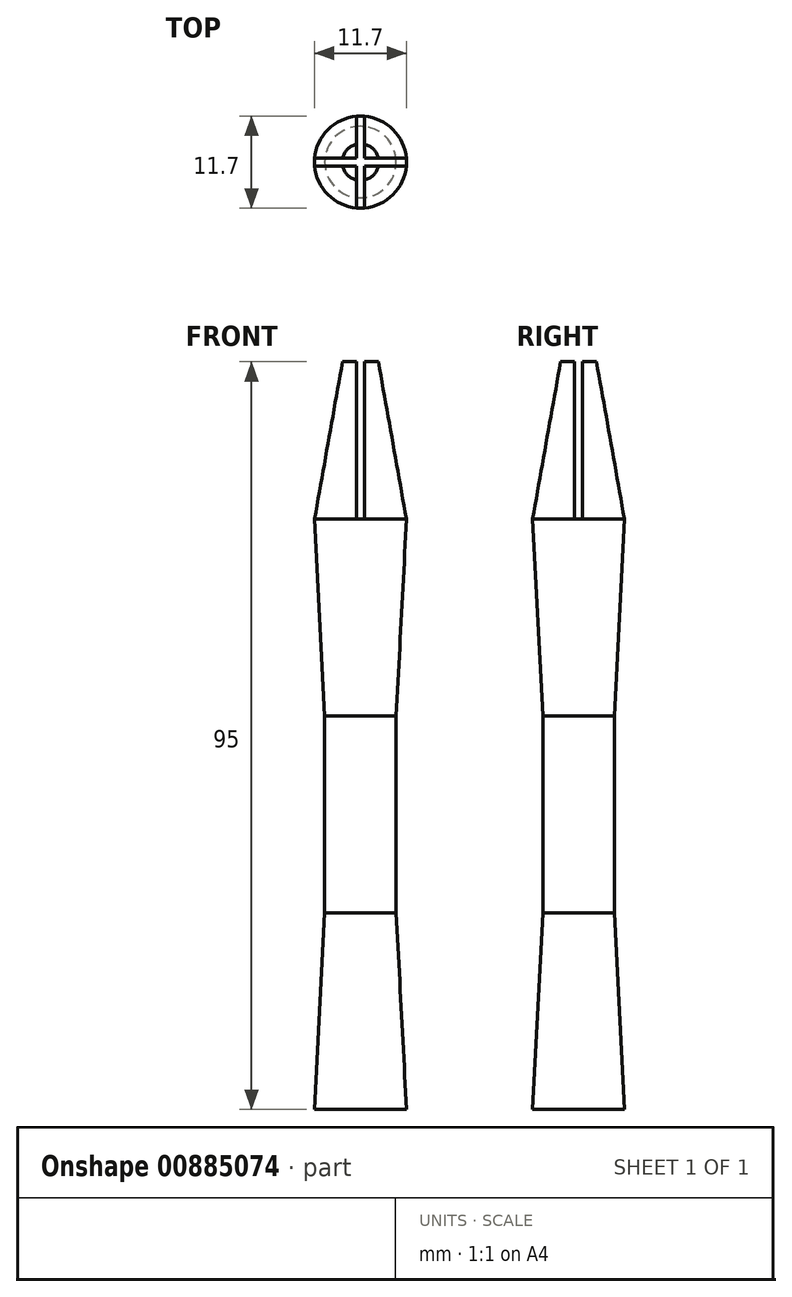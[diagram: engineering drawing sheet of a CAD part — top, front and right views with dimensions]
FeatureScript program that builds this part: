
annotation { "Feature Type Name" : "Feature", "Feature Type Description" : "" }
export const myFeature = defineFeature(function(context is Context, id is Id, definition is map)
    precondition{}
    {
        {
            var Q0;
            Q0=qCreatedBy(makeId("Top.planeOp"),FACE);
            var sketch = newSketch(context, id + "F0", { "sketchPlane" : qUnion([Q0])});
            skCircle(sketch, "E0", {"center": v(0, 0) * mm, "radius": 5.85 * mm});
            skSolve(sketch);
        }
        {
            var Q0;
            Q0=makeQuery(id+"F0.imprint","IMPRINT",FACE,{"disambiguationData":[TD([[makeQuery(id+"F0.imprint","IMPRINT",EDGE,{"derivedFrom":sQuery(id+"F0.wireOp",EDGE,"E0")}),1.0]])]});
            var Q1;
            Q1=sQuery(id+"F0.wireOp",EDGE,"E0");
            extrude(context, id + "F1", {"entities" : qUnion([Q0]), "surfaceEntities" : qUnion([Q1]), "depth" : 25 * mm, "offsetDistance" : 25 * mm, "hasDraft" : true, "draftAngle" : 3 * degree, "draftPullDirection" : true});
        }
        {
            var Q0;
            Q0=makeQuery(id+"F1.opExtrude","CAP_FACE",FACE,{"disambiguationData":[OSD([sQuery(id+"F0.wireOp",EDGE,"E0")])],"isStart":false});
            extrude(context, id + "F2", {"entities" : qUnion([Q0]), "operationType" : NewBodyOperationType.ADD, "depth" : 25 * mm, "offsetDistance" : 25 * mm});
        }
        {
            var Q0;
            Q0=makeQuery(id+"F2.opExtrude","CAP_FACE",FACE,{"disambiguationData":[OSD([sQuery(id+"F0.wireOp",EDGE,"E0")])],"isStart":false});
            extrude(context, id + "F3", {"entities" : qUnion([Q0]), "operationType" : NewBodyOperationType.ADD, "depth" : 25 * mm, "offsetDistance" : 25 * mm, "hasDraft" : true, "draftAngle" : 3 * degree});
        }
        {
            var Q0;
            Q0=makeQuery(id+"F3.opExtrude","CAP_FACE",FACE,{"disambiguationData":[OSD([sQuery(id+"F0.wireOp",EDGE,"E0")])],"isStart":false});
            extrude(context, id + "F4", {"entities" : qUnion([Q0]), "operationType" : NewBodyOperationType.ADD, "depth" : 20 * mm, "offsetDistance" : 25 * mm, "hasDraft" : true, "draftAngle" : 10 * degree, "draftPullDirection" : true});
        }
        {
            var Q0;
            Q0=makeQuery(id+"F4.opExtrude","CAP_FACE",FACE,{"disambiguationData":[OSD([sQuery(id+"F0.wireOp",EDGE,"E0")])],"isStart":false});
            var sketch = newSketch(context, id + "F5", { "sketchPlane" : qUnion([Q0])});
            skLineSegment(sketch, "E1.bottom", {"start": v(-10.12, -0.5) * mm, "end": v(10.12, -0.5) * mm});
            skLineSegment(sketch, "E1.top", {"start": v(-10.12, 0.5) * mm, "end": v(10.12, 0.5) * mm});
            skLineSegment(sketch, "E1.left", {"start": v(-10.12, -0.5) * mm, "end": v(-10.12, 0.5) * mm});
            skLineSegment(sketch, "E1.right", {"start": v(10.12, -0.5) * mm, "end": v(10.12, 0.5) * mm});
            skPoint(sketch, "E1.middle", {"position": v(0, 0) * mm});
            skLineSegment(sketch, "E2.bottom", {"start": v(0.5, 11.68) * mm, "end": v(-0.5, 11.68) * mm});
            skLineSegment(sketch, "E2.top", {"start": v(0.5, -11.68) * mm, "end": v(-0.5, -11.68) * mm});
            skLineSegment(sketch, "E2.left", {"start": v(0.5, 11.68) * mm, "end": v(0.5, -11.68) * mm});
            skLineSegment(sketch, "E2.right", {"start": v(-0.5, 11.68) * mm, "end": v(-0.5, -11.68) * mm});
            skSolve(sketch);
        }
        {
            var Q0;
            {var subQ0=sQuery(id+"F5.wireOp",EDGE,"E2.right");var subQ1=sQuery(id+"F5.wireOp",EDGE,"E1.top");var subQ2=makeQuery(id+"F5.imprint","INTERSECT",VERTEX,{"derivedFrom":[subQ1,subQ0]});Q0=makeQuery(id+"F5.imprint","IMPRINT",FACE,{"disambiguationData":[TD([[makeQuery(id+"F5.imprint","IMPRINT",EDGE,{"disambiguationData":[TD([[subQ2,-1.0]])],"derivedFrom":subQ1}),1.0]])]});}
            var Q1;
            {var subQ0=sQuery(id+"F5.wireOp",EDGE,"E2.right");var subQ1=sQuery(id+"F5.wireOp",EDGE,"E1.bottom");var subQ2=makeQuery(id+"F5.imprint","INTERSECT",VERTEX,{"derivedFrom":[subQ1,subQ0]});Q1=makeQuery(id+"F5.imprint","IMPRINT",FACE,{"disambiguationData":[TD([[makeQuery(id+"F5.imprint","IMPRINT",EDGE,{"disambiguationData":[TD([[subQ2,1.0]])],"derivedFrom":subQ1}),1.0]])]});}
            var Q2;
            {var subQ0=sQuery(id+"F5.wireOp",EDGE,"E2.right");var subQ1=sQuery(id+"F5.wireOp",EDGE,"E1.bottom");var subQ2=makeQuery(id+"F5.imprint","INTERSECT",VERTEX,{"derivedFrom":[subQ1,subQ0]});Q2=makeQuery(id+"F5.imprint","IMPRINT",FACE,{"disambiguationData":[TD([[makeQuery(id+"F5.imprint","IMPRINT",EDGE,{"disambiguationData":[TD([[subQ2,-1.0]])],"derivedFrom":subQ1}),-1.0]])]});}
            var Q3;
            {var subQ0=sQuery(id+"F5.wireOp",EDGE,"E2.left");var subQ1=sQuery(id+"F5.wireOp",EDGE,"E1.bottom");var subQ2=makeQuery(id+"F5.imprint","INTERSECT",VERTEX,{"derivedFrom":[subQ1,subQ0]});Q3=makeQuery(id+"F5.imprint","IMPRINT",FACE,{"disambiguationData":[TD([[makeQuery(id+"F5.imprint","IMPRINT",EDGE,{"disambiguationData":[TD([[subQ2,-1.0]])],"derivedFrom":subQ1}),1.0]])]});}
            var Q4;
            {var subQ0=sQuery(id+"F5.wireOp",EDGE,"E2.right");var subQ1=sQuery(id+"F5.wireOp",EDGE,"E1.bottom");var subQ2=makeQuery(id+"F5.imprint","INTERSECT",VERTEX,{"derivedFrom":[subQ1,subQ0]});Q4=makeQuery(id+"F5.imprint","IMPRINT",FACE,{"disambiguationData":[TD([[makeQuery(id+"F5.imprint","IMPRINT",EDGE,{"disambiguationData":[TD([[subQ2,-1.0]])],"derivedFrom":subQ1}),1.0]])]});}
            var Q5;
            {var subQ0=sQuery(id+"F5.wireOp",EDGE,"E1.left");Q5=makeQuery(id+"F5.imprint","IMPRINT",FACE,{"disambiguationData":[TD([[makeQuery(id+"F5.imprint","IMPRINT",EDGE,{"derivedFrom":subQ0}),-1.0]])]});}
            var Q6;
            {var subQ0=sQuery(id+"F5.wireOp",EDGE,"E2.top");Q6=makeQuery(id+"F5.imprint","IMPRINT",FACE,{"disambiguationData":[TD([[makeQuery(id+"F5.imprint","IMPRINT",EDGE,{"derivedFrom":subQ0}),-1.0]])]});}
            var Q7;
            {var subQ0=sQuery(id+"F5.wireOp",EDGE,"E1.right");Q7=makeQuery(id+"F5.imprint","IMPRINT",FACE,{"disambiguationData":[TD([[makeQuery(id+"F5.imprint","IMPRINT",EDGE,{"derivedFrom":subQ0}),1.0]])]});}
            var Q8;
            {var subQ0=sQuery(id+"F5.wireOp",EDGE,"E2.bottom");Q8=makeQuery(id+"F5.imprint","IMPRINT",FACE,{"disambiguationData":[TD([[makeQuery(id+"F5.imprint","IMPRINT",EDGE,{"derivedFrom":subQ0}),1.0]])]});}
            extrude(context, id + "F6", {"entities" : qUnion([Q0, Q1, Q2, Q3, Q4, Q5, Q6, Q7, Q8]), "operationType" : NewBodyOperationType.REMOVE, "oppositeDirection" : true, "depth" : 20 * mm, "offsetDistance" : 25 * mm});
        }
    });
